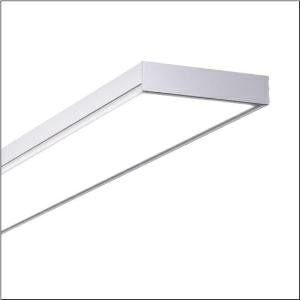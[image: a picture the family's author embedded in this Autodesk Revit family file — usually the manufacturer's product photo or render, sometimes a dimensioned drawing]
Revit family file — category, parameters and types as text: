
# Revit family: apollon_31_surface_51mp26wm2341e
name_source: partatom
category: Lighting Fixtures
units: mm (PartAtom-declared; Revit-internal decimal feet)

## family parameters
Cut with Voids When Loaded = No
Host = Face
Light Source = No
Part Type = Normal
Room Calculation Point = No
Round Connector Dimension = Use Diameter
Shared = No

## types (1)
- Apollon 31 Surface (1 x LED, 4400 lm, 33 W, 3000K)
    Apparent Load = 33 VA
    CIE Flux Codes = 61 87 97 97 100
    Color Rendering = 80
    Color Temperature = 3000K
    Default Elevation = 1800 mm
    Description = Apollon 31 Surface, office luminaire, primary optical cover: micro prismatic cover, of PMMA, light emission: direct distribution, primary light characteristic: symmetric, installation type: surface-mounted, LED, rated luminous flux: 4.400lm, luminous efficacy: 133lm/W, light colour: 830, colour temperature: 3000K, control gear: ON/OFF Multilumen, with terminal, 3-pole, mains connection: 220..240V, AC, 50/60Hz, rated input power: 33W, housing, of sheet steel, coated, metallic grey (RAL 9006), length: 1.545mm, width: 200mm, height: 44mm, protection rating (complete): IP20, protection rating (on room side): IP40, protection rating (lamp compartment, on room side): IP40, insulation class (complete): insulation class I (protective earthing), certification: CE, ENEC, UKCA, impact resistance: IK02, permissible operating ambient temperature: -20..+40°C, packaging unit: 1 piece
    Height = 44 mm
    Lamp = 1 x LED
    Lamp Light Flux = 4400 lm
    Lamp Power = 33 W
    Lamp count = 1
    Length = 1545 mm
    Luminous efficacy = 133 lm/W
    Manufacturer = Siteco
    ModVariant = No
    Model = 51MP26WM2341E
    Mounting Place = Ceiling
    Mounting Type = Surface mounted
    Number of Poles = 1
    OnlyDefault = Yes
    Power Factor = 1
    Product Name = Apollon 31 Surface
    Product group = office luminaire | ceiling mounted
    ProductGroupID = 301
    Protection Class = Protection class I
    Protection Degree = IP 20
    RLX_Detail_Level = 1
    RLX_Emergency_Light_Flux = 0 lm
    RLX_Emergency_Type = 0
    RLX_Emergency_Type_DB = No
    RlxData = <blob elided: 24129 chars, md5=7da8a64f>
    Socket = socket
    Standby Power = 0 W
    System Light Flux = 4400 lm
    System Power = 33 W
    Type Comments = Product without accessories
    Type Image = l_1313654.jpg
    URL = http://relux.com
    VarID = ---
    Voltage = 0 V
    Weight = 0.00 kg
    Width = 200 mm  [stored 0.656168 ft]

note: [stored X ft] marks values corroborated as IEEE doubles in the binary element streams (Revit-internal decimal feet)

## geometry (parser evidence)
native form markers: Blend x4, Sweep x12
no freeform markers — native parametric forms only
